# Revit family: TYCO-FPP-FireClass-FC410BDM BEAM DETECTOR MODULE
name_source: partatom
category: Electrical Fixtures
revit_build: Autodesk Revit 2014 (Build: 20130308_1515(x64)
units: mm (PartAtom-declared; Revit-internal decimal feet)

## types (1)
- TYCO-FPP-FireClass-FC410BDM BEAM DETECTOR MODULE
    Description = Beam Detector
    Detector EOL = 4k7 Ohm
    Front Cover = Yes
    Keynote = The FC410BDM Beam Detector Interface Module is designed to
power and interface one FIRERAY 50/100/2000/5000 Beam
Detector to the FireClass Digital Addressable Loop.
    Length = 48 mm
    Loop Voltage = 20V to 40Vdc
    Manufacturer = Tyco
    Model = FireClass- 555.800.766
    Operating Temperature = 10 - + 55 ºC
    PCB = PCB
    Rear Cover = Yes
    Relative Humidity = 10% to 95%
    Storage Temperature = –40°C to +80°C
    Type Comments = For remote siting of the FIRERAY
detector an optional BTM800 Terminal Module can be used.
    Typical Alarm mA = 21
    Typical Standby mA = 14
    URL = https://fireclass.co.uk
    Width = 57 mm

## geometry (parser evidence)
native form markers: Sweep x6
no freeform markers — native parametric forms only
